# Revit family: KINGSLEY Mini Hob Spout – BRUSHED BRASS (SKU 14020)
name_source: partatom
category: Plumbing Fixtures
units: mm (PartAtom-declared; Revit-internal decimal feet)

## family parameters
Always vertical = Yes
Cut with Voids When Loaded = No
Maintain Annotation Orientation = No
OmniClass Number = 23.45.55.14
OmniClass Title = Single Faucets
Part Type = Normal
Room Calculation Point = No
Round Connector Dimension = Use Diameter
Shared = No
Work Plane-Based = No

## types (1)
- KINGSLEY MINI HOB SPOUT – BRUSHED BRASS (SKU 14020)
    CW Connection = No
    Default Elevation = 0 mm  [stored 0 ft]
    Description = KINGSLEY Mini Hob Spout – BRUSHED BRASS (SKU 14020)
    HW Connection = No
    Manufacturer = ABI Interiors PTY LTD
    Model = BRUSHED BRASS (SKU 14020)
    URL = https://www.abiinteriors.com.au
    Vent Connection = No
    Waste Connection = No

note: [stored X ft] marks values corroborated as IEEE doubles in the binary element streams (Revit-internal decimal feet)

## geometry (parser evidence)
native form markers: Sweep x3
no freeform markers — native parametric forms only
